# Revit family: Robe-Hook_Traditional_Guinevere_YH970_TOTO
name_source: partatom
category: Furniture
revit_build: Autodesk Revit Architecture 2013 (Build: 20130531_2115(x64)
units: mm (PartAtom-declared; Revit-internal decimal feet)

## types (1)
- YH784
    04 CSI = 10 28 00
    95 CSI = 10800
    Assembly Code = C1030200
    CAD Drawing URL = http://assets.totousa.com
    Color Availability = #CP  Polished Chrome, #BN  Brushed Nickel, #PN  Polished Nickel, #RB Oil Rubbed Bronze
    Default Elevation = 0"
    Depth = 3 13/32"
    Description = Robe Hook
    Finish = Metal - TOTO - Chrome - Polished
    Height = 3 1/8"
    Manufacturer = TOTO USA, Inc.
    Manufacturer Fax = (770) 282-0002
    Model = YH970
    Series = Guinevere
    Shipping Weight = 0.50 lb
    Spec Sheet URL = http://assets.totousa.com
    Style = Traditional
    Subcategory = Accessories
    Toto BIM Number = BM-00226
    URL = http://www.totousa.com
    Warranty = Lifetime Limited Warranty (Residential Use), One Year (Oil Rubbed Bronze), One Year Limited (Commercial Use)
    Warranty URL = http://www.totousa.com
    Width = 1 27/32"

## geometry (parser evidence)
native form markers: Blend x16, Sweep x3
no freeform markers — native parametric forms only
